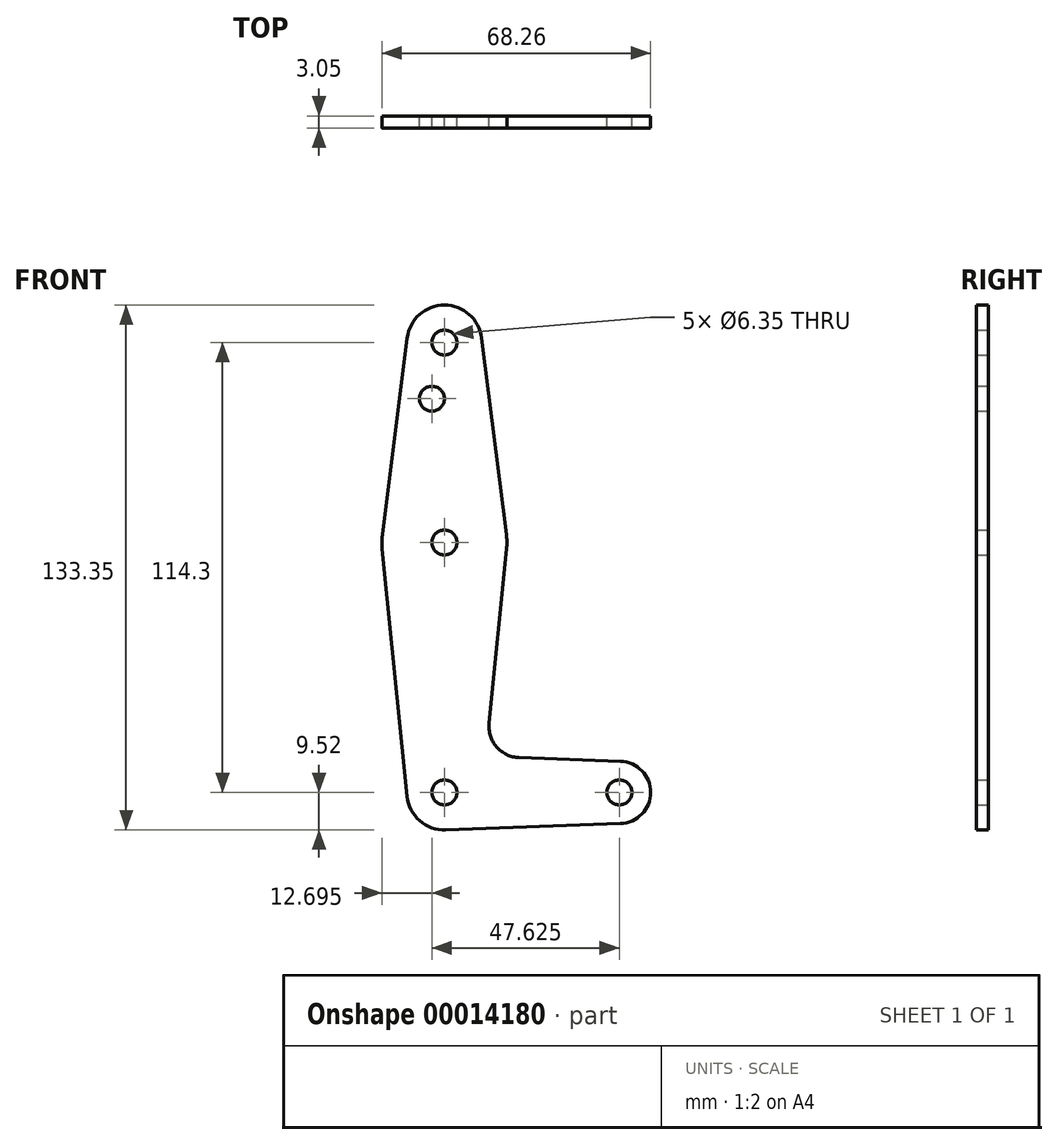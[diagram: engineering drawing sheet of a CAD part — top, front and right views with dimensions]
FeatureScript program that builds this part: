
annotation { "Feature Type Name" : "Feature", "Feature Type Description" : "" }
export const myFeature = defineFeature(function(context is Context, id is Id, definition is map)
    precondition{}
    {
        {
            var Q0;
            Q0=qCreatedBy(makeId("Front.planeOp"),FACE);
            var sketch = newSketch(context, id + "F0", { "sketchPlane" : qUnion([Q0])});
            skLineSegment(sketch, "E0", {"start": v(44.45, 0) * mm, "end": v(0, 0) * mm, "construction": true});
            skLineSegment(sketch, "E1", {"start": v(0, 0) * mm, "end": v(0, 114.3) * mm, "construction": true});
            skCircle(sketch, "E2", {"center": v(44.45, 0) * mm, "radius": 7.94 * mm});
            skCircle(sketch, "E3", {"center": v(0, 0) * mm, "radius": 9.53 * mm});
            skCircle(sketch, "E4", {"center": v(0, 63.5) * mm, "radius": 15.88 * mm});
            skCircle(sketch, "E5", {"center": v(0, 114.3) * mm, "radius": 9.53 * mm});
            skLineSegment(sketch, "E6", {"start": v(-9.48, -0.95) * mm, "end": v(-15.8, 61.91) * mm});
            skLineSegment(sketch, "E7", {"start": v(15.8, 61.91) * mm, "end": v(11.34, 17.6) * mm});
            skLineSegment(sketch, "E8", {"start": v(-15.75, 65.48) * mm, "end": v(-9.45, 115.5) * mm});
            skLineSegment(sketch, "E9", {"start": v(15.75, 65.48) * mm, "end": v(9.45, 115.5) * mm});
            skCircle(sketch, "E10", {"center": v(0, 114.3) * mm, "radius": 3.18 * mm});
            skCircle(sketch, "E11", {"center": v(0, 63.5) * mm, "radius": 3.18 * mm});
            skCircle(sketch, "E12", {"center": v(0, 0) * mm, "radius": 3.18 * mm});
            skCircle(sketch, "E13", {"center": v(44.45, 0) * mm, "radius": 3.18 * mm});
            skCircle(sketch, "E14", {"center": v(-3.18, 100.03) * mm, "radius": 3.18 * mm});
            skLineSegment(sketch, "E15", {"start": v(0.34, -9.52) * mm, "end": v(44.73, -7.93) * mm});
            skLineSegment(sketch, "E16", {"start": v(44.73, 7.93) * mm, "end": v(18.97, 8.85) * mm});
            skArc(sketch, "E17.filletArc", {"start": v(11.34, 17.6) * mm, "mid": v(13.26, 11.57) * mm, "end": v(18.97, 8.85) * mm});
            skSolve(sketch);
        }
        {
            var Q0;
            Q0 = qSketchRegion(id + "F0", true);
            extrude(context, id + "F1", {"entities" : qUnion([Q0]), "depth" : 3.05 * mm});
        }
    });
